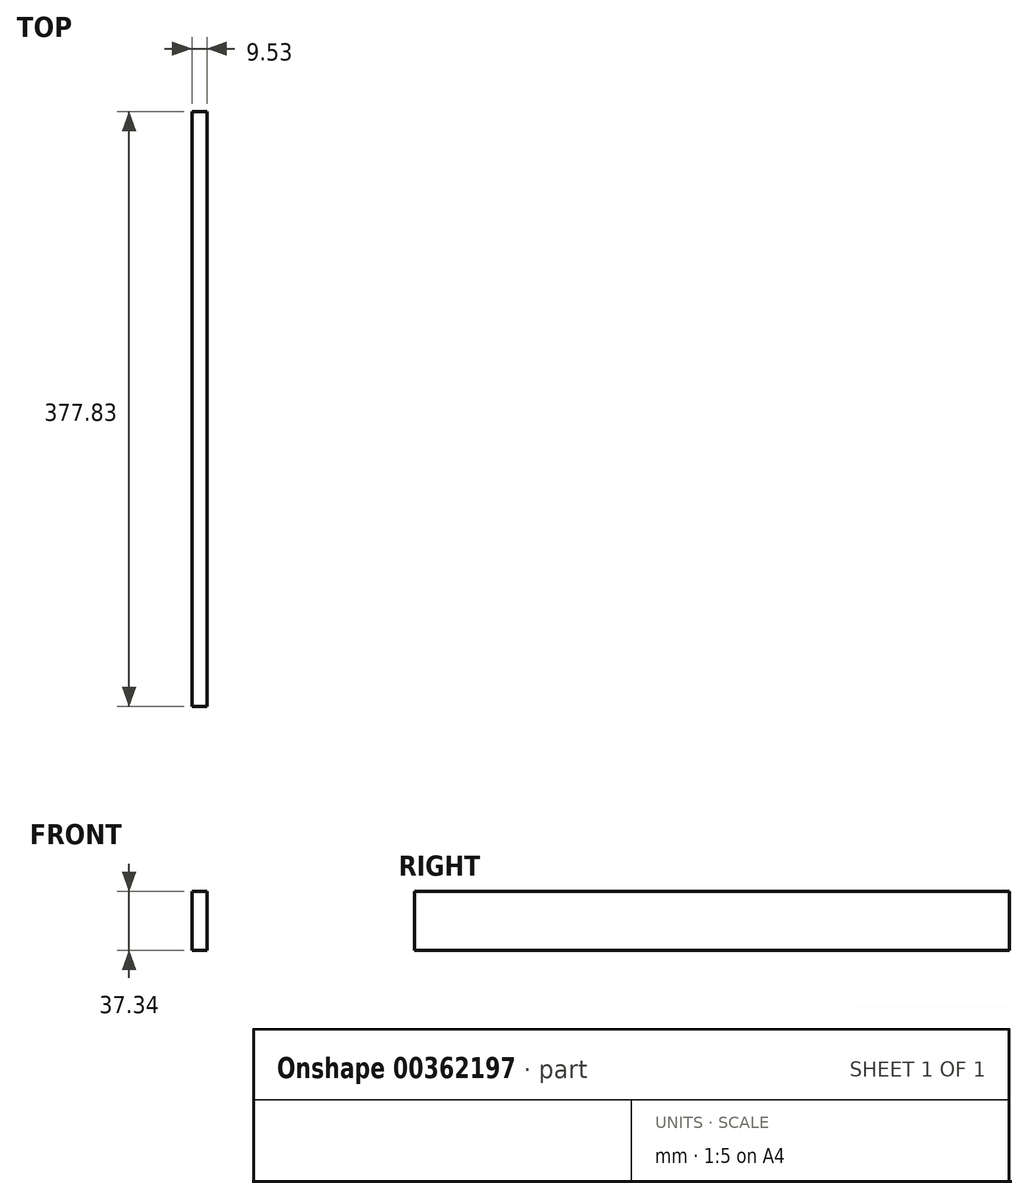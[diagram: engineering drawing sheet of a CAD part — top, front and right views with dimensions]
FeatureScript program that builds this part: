
annotation { "Feature Type Name" : "Feature", "Feature Type Description" : "" }
export const myFeature = defineFeature(function(context is Context, id is Id, definition is map)
    precondition{}
    {
        {
            var Q0;
            Q0=qCreatedBy(makeId("Right.planeOp"),FACE);
            var sketch = newSketch(context, id + "F0", { "sketchPlane" : qUnion([Q0])});
            skLineSegment(sketch, "E0.bottom", {"start": v(0, 0) * mm, "end": v(377.83, 0) * mm});
            skLineSegment(sketch, "E0.top", {"start": v(0, 37.34) * mm, "end": v(377.83, 37.34) * mm});
            skLineSegment(sketch, "E0.left", {"start": v(0, 0) * mm, "end": v(0, 37.34) * mm});
            skLineSegment(sketch, "E0.right", {"start": v(377.83, 0) * mm, "end": v(377.83, 37.34) * mm});
            skSolve(sketch);
        }
        {
            var Q0;
            Q0 = qSketchRegion(id + "F0", true);
            extrude(context, id + "F1", {"entities" : qUnion([Q0]), "depth" : 9.52 * mm});
        }
    });
